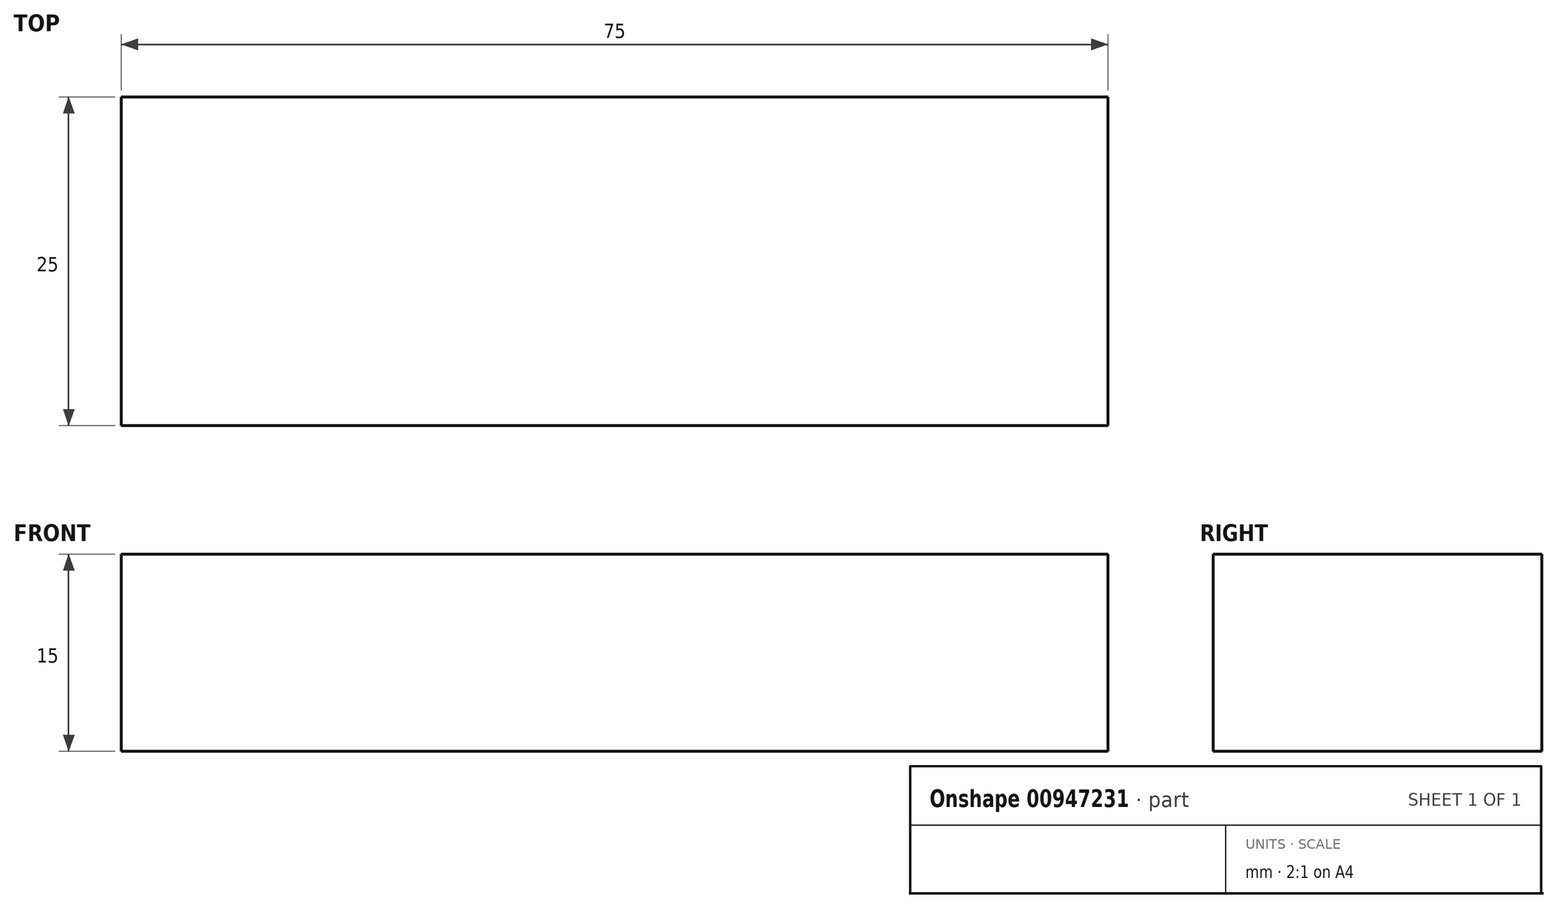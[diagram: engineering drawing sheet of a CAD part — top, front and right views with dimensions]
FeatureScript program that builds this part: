
annotation { "Feature Type Name" : "Feature", "Feature Type Description" : "" }
export const myFeature = defineFeature(function(context is Context, id is Id, definition is map)
    precondition{}
    {
        {
            var Q0;
            Q0=qCreatedBy(makeId("Front.planeOp"),FACE);
            var sketch = newSketch(context, id + "F0", { "sketchPlane" : qUnion([Q0])});
            skLineSegment(sketch, "E0.bottom", {"start": v(-67.34, 8.08) * mm, "end": v(7.66, 8.08) * mm});
            skLineSegment(sketch, "E0.top", {"start": v(-67.34, 23.08) * mm, "end": v(7.66, 23.08) * mm});
            skLineSegment(sketch, "E0.left", {"start": v(-67.34, 8.08) * mm, "end": v(-67.34, 23.08) * mm});
            skLineSegment(sketch, "E0.right", {"start": v(7.66, 8.08) * mm, "end": v(7.66, 23.08) * mm});
            skSolve(sketch);
        }
        {
            var Q0;
            Q0 = qSketchRegion(id + "F0", true);
            extrude(context, id + "F1", {"entities" : qUnion([Q0]), "depth" : 25 * mm, "offsetDistance" : 25 * mm});
        }
    });
